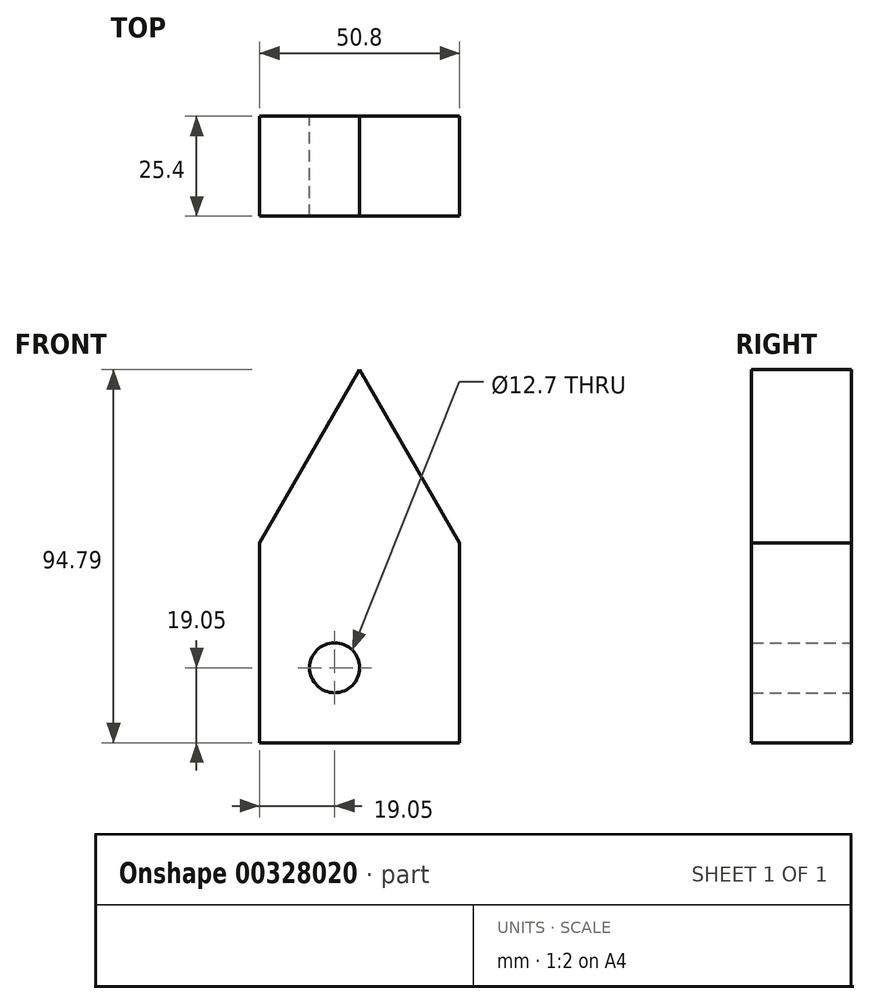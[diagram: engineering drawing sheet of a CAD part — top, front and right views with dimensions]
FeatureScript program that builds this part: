
annotation { "Feature Type Name" : "Feature", "Feature Type Description" : "" }
export const myFeature = defineFeature(function(context is Context, id is Id, definition is map)
    precondition{}
    {
        {
            var Q0;
            Q0=qCreatedBy(makeId("Front.planeOp"),FACE);
            var sketch = newSketch(context, id + "F0", { "sketchPlane" : qUnion([Q0])});
            skLineSegment(sketch, "E0.bottom", {"start": v(25.4, -25.4) * mm, "end": v(-25.4, -25.4) * mm});
            skLineSegment(sketch, "E0.top", {"start": v(25.4, 25.4) * mm, "end": v(-25.4, 25.4) * mm});
            skLineSegment(sketch, "E0.left", {"start": v(25.4, -25.4) * mm, "end": v(25.4, 25.4) * mm});
            skLineSegment(sketch, "E0.right", {"start": v(-25.4, -25.4) * mm, "end": v(-25.4, 25.4) * mm});
            skPoint(sketch, "E0.middle", {"position": v(0, 0) * mm});
            skLineSegment(sketch, "E1", {"start": v(-25.4, 25.4) * mm, "end": v(0, 69.4) * mm});
            skLineSegment(sketch, "E2", {"start": v(0, 69.4) * mm, "end": v(25.4, 25.4) * mm});
            skLineSegment(sketch, "E3.bottom", {"start": v(-25.4, -25.4) * mm, "end": v(-6.35, -25.4) * mm});
            skLineSegment(sketch, "E3.left", {"start": v(-25.4, -25.4) * mm, "end": v(-25.4, -6.35) * mm});
            skCircle(sketch, "E4", {"center": v(-6.35, -6.35) * mm, "radius": 6.35 * mm});
            skSolve(sketch);
        }
        {
            var Q0;
            Q0 = qSketchRegion(id + "F0", true);
            extrude(context, id + "F1", {"entities" : qUnion([Q0]), "depth" : 25.4 * mm});
        }
    });
